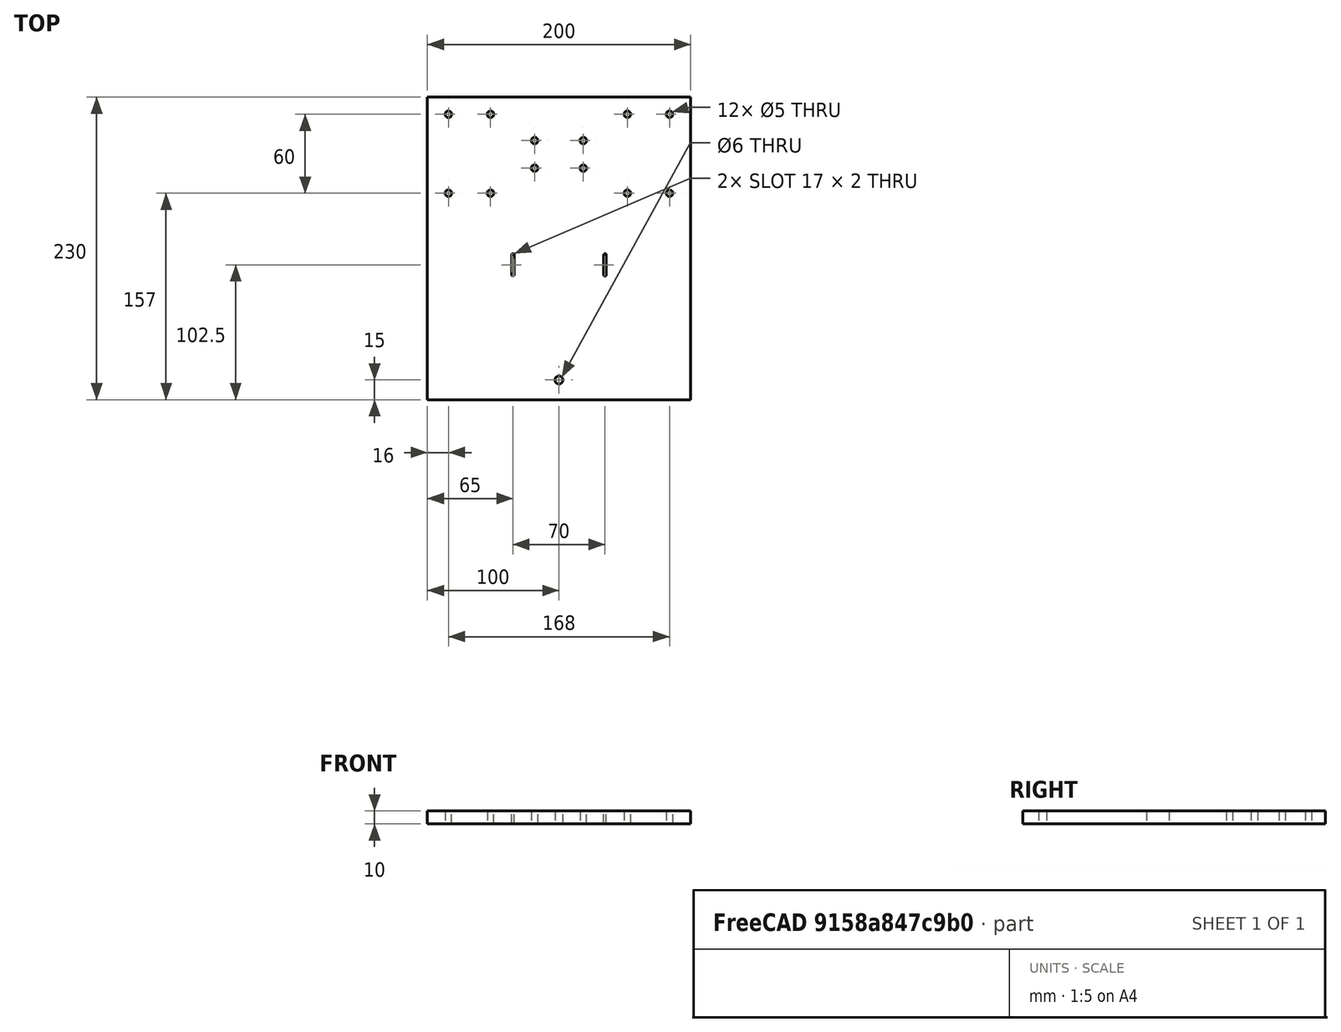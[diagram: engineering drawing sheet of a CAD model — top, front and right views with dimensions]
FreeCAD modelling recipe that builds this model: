
FCSTD DOCUMENT  (FreeCAD 0.15R4664 (Git))
Label: platez_base
License: CC-BY 3.0
LicenseURL: http://creativecommons.org/licenses/by/3.0/
objects: Drawing::FeatureView×38, Sketcher::SketchObject×1, PartDesign::Pad×1, Drawing::FeatureViewPart×1, Drawing::FeaturePage×1
note: 3 computed .brp shape members not serialized (recipe doc carries the construction recipe); baked Part::Feature solids carry a one-line shape summary decoded from their .brp

FEATURE [Sketcher::SketchObject] Sketch
  sketch-geometry (25):
    g0: LineSegment StartX=-100 StartY=230 StartZ=0 EndX=100 EndY=230 EndZ=0
    g1: LineSegment StartX=100 StartY=230 StartZ=0 EndX=100 EndY=0 EndZ=0
    g2: LineSegment StartX=100 StartY=0 StartZ=0 EndX=-100 EndY=0 EndZ=0
    g3: LineSegment StartX=-100 StartY=0 StartZ=0 EndX=-100 EndY=230 EndZ=0
    g4: Circle CenterX=0 CenterY=15 CenterZ=0 NormalX=0 NormalY=0 NormalZ=1 Radius=3
    g5: ArcOfCircle CenterX=35 CenterY=110 CenterZ=0 NormalX=0 NormalY=0 NormalZ=1 Radius=1 StartAngle=4.4411e-08 EndAngle=3.14159
    g6: LineSegment StartX=36 StartY=110 StartZ=0 EndX=36 EndY=95 EndZ=0
    g7: LineSegment StartX=34 StartY=110 StartZ=0 EndX=34 EndY=95 EndZ=0
    g8: ArcOfCircle CenterX=35 CenterY=95 CenterZ=0 NormalX=0 NormalY=0 NormalZ=1 Radius=1 StartAngle=3.14159 EndAngle=6.28319
    g9: ArcOfCircle CenterX=-35 CenterY=110 CenterZ=0 NormalX=0 NormalY=0 NormalZ=1 Radius=1 StartAngle=6.28319 EndAngle=9.42478
    g10: LineSegment StartX=-34 StartY=110 StartZ=0 EndX=-34 EndY=95 EndZ=0
    g11: LineSegment StartX=-36 StartY=110 StartZ=0 EndX=-36 EndY=95 EndZ=0
    g12: ArcOfCircle CenterX=-35 CenterY=95 CenterZ=0 NormalX=0 NormalY=0 NormalZ=1 Radius=1 StartAngle=3.14159 EndAngle=6.28319
    g13: Circle CenterX=84 CenterY=217 CenterZ=0 NormalX=0 NormalY=0 NormalZ=1 Radius=2.5
    g14: Circle CenterX=84 CenterY=157 CenterZ=0 NormalX=0 NormalY=0 NormalZ=1 Radius=2.5
    g15: Circle CenterX=52 CenterY=157 CenterZ=0 NormalX=0 NormalY=0 NormalZ=1 Radius=2.5
    g16: Circle CenterX=52 CenterY=217 CenterZ=0 NormalX=0 NormalY=0 NormalZ=1 Radius=2.5
    g17: Circle CenterX=-84 CenterY=217 CenterZ=0 NormalX=0 NormalY=0 NormalZ=1 Radius=2.5
    g18: Circle CenterX=-52 CenterY=217 CenterZ=0 NormalX=0 NormalY=0 NormalZ=1 Radius=2.5
    g19: Circle CenterX=-84 CenterY=157 CenterZ=0 NormalX=0 NormalY=0 NormalZ=1 Radius=2.5
    g20: Circle CenterX=-52 CenterY=157 CenterZ=0 NormalX=0 NormalY=0 NormalZ=1 Radius=2.5
    g21: Circle CenterX=-18.5 CenterY=197 CenterZ=0 NormalX=0 NormalY=0 NormalZ=1 Radius=2.5
    g22: Circle CenterX=18.5 CenterY=197 CenterZ=0 NormalX=0 NormalY=0 NormalZ=1 Radius=2.5
    g23: Circle CenterX=-18.5 CenterY=176 CenterZ=0 NormalX=0 NormalY=0 NormalZ=1 Radius=2.5
    g24: Circle CenterX=18.5 CenterY=176 CenterZ=0 NormalX=0 NormalY=0 NormalZ=1 Radius=2.5
  constraints (78):
    c: Coincident(g0,g1)
    c: Coincident(g1,g2)
    c: Coincident(g2,g3)
    c: Coincident(g3,g0)
    c: Horizontal(g0)
    c: Horizontal(g2)
    c: Vertical(g1)
    c: Vertical(g3)
    c: PointOnObject(g1,g-1)
    c: Distance(g2,g1) = 200
    c: Distance(g-1,g2) = 100
    c: Distance(g0,g1) = 230
    c: Radius(g4) = 3
    c: PointOnObject(g4,g-2)
    c: Distance(g-1,g4) = 15
    c: Radius(g5) = 1
    c: Coincident(g6,g5)
    c: Vertical(g6)
    c: Tangent(g6,g5)
    c: Coincident(g7,g5)
    c: Vertical(g7)
    c: Tangent(g7,g5)
    c: Coincident(g8,g7)
    c: Coincident(g8,g6)
    c: Radius(g8) = 1
    c: Distance(g7) = 15
    c: Distance(g7,g6) = 2
    c: Distance(g6,g1) = 64
    c: Distance(g6,g2) = 95
    c: Coincident(g10,g9)
    c: Vertical(g10)
    c: Tangent(g10,g9)
    c: Radius(g9) = 1
    c: Coincident(g11,g9)
    c: Vertical(g11)
    c: Tangent(g11,g9)
    c: Coincident(g12,g11)
    c: Coincident(g12,g10)
    c: Radius(g12) = 1
    c: Distance(g11,g10) = 2
    c: Distance(g10,g2) = 95
    c: Distance(g11,g3) = 64
    c: Radius(g13) = 2.5
    c: Distance(g13,g1) = 16
    c: Distance(g13,g0) = 13
    c: Radius(g14) = 2.5
    c: DistanceY(g13,g14) = -60
    c: Distance(g14,g1) = 16
    c: Radius(g15) = 2.5
    c: DistanceX(g15,g14) = 32
    c: Radius(g16) = 2.5
    c: DistanceX(g16,g13) = 32
    c: Distance(g16,g0) = 13
    c: DistanceY(g16,g15) = -60
    c: Radius(g17) = 2.5
    c: Distance(g17,g0) = 13
    c: Distance(g17,g3) = 16
    c: Radius(g18) = 2.5
    c: Distance(g18,g0) = 13
    c: DistanceY(g17,g19) = -60
    c: Distance(g19,g3) = 16
    c: DistanceY(g18,g20) = -60
    c: DistanceX(g19,g20) = 32
    c: DistanceX(g17,g18) = 32
    c: Radius(g19) = 2.5
    c: Radius(g20) = 2.5
    c: Radius(g21) = 2.5
    c: Radius(g22) = 2.5
    c: Radius(g23) = 2.5
    c: Radius(g24) = 2.5
    c: Distance(g21,g23) = 21
    c: Distance(g22,g24) = 21
    c: Distance(g21,g0) = 33
    c: Distance(g22,g0) = 33
    c: Distance(g21,g3) = 81.5
    c: Distance(g23,g3) = 81.5
    c: Distance(g22,g1) = 81.5
    c: Distance(g24,g1) = 81.5
FEATURE [PartDesign::Pad] Pad
  Length = 10
  Length2 = 1
  Sketch = -> Sketch
  Type = 0
FEATURE [Drawing::FeatureViewPart] View
  Direction = (0,0,1)
  HiddenWidth = 0.15
  LineWidth = 0.35
  Rotation = 0
  Scale = 0.5
  ShowHiddenLines = false
  ShowSmoothLines = false
  Source = -> Pad
  Tolerance = 0.05
  ViewResult = <g id="View"\n   transform="rotate(0,150,140) translate(150,140) scale(0.5,0.5)"\n  >\n<g   stroke="rgb(0, 0, 0)"\n   stroke-width="0.7"\n   stroke-linecap="butt"\n   stroke-linejoin="miter"\n   fill="none"\n   transform="scale(1,-1)"\n  >\n<path id= "1" d=" M -100 230 L 100 230 " />\n<path id= "2" d=" M 100 230 L 100 0 " />\n<path id= "3" d=" M 100 0 L -100 0 " />\n<path id= "4" d=" M -100 0 L -100 230 " />\n<path d="M36 110 A1 1 0 1 1 34 110" /><path id= "6" d=" M 34 110 L 34 95 " />\n<path d="M34 95 A1 1 0 1 1 36 95" /><path id= "8" d=" M 36 110 L 36 95 " />\n<path d="M-34 110 A1 1 0 1 1 -36 110" /><path id= "10" d=" M -36 110 L -36 95 " />\n<path d="M-36 95 A1 1 0 0 1 -34 95" /><path id= "12" d=" M -34 110 L -34 95 " />\n<circle cx ="0" cy ="15" r ="3" /><circle cx ="-52" cy ="157" r ="2.5" /><circle cx ="-84" cy ="157" r ="2.5" /><circle cx ="-52" cy ="217" r ="2.5" /><circle cx ="-84" cy ="217" r ="2.5" /><circle cx ="52" cy ="217" r ="2.5" /><circle cx ="52" cy ="157" r ="2.5" /><circle cx ="84" cy ="157" r ="2.5" /><circle cx ="84" cy ="217" r ="2.5" /><circle cx ="18.5" cy ="176" r ="2.5" /><circle cx ="-18.5" cy ="176" r ="2.5" /><circle cx ="18.5" cy ="197" r ="2.5" /><circle cx ="-18.5" cy ="197" r ="2.5" /></g>\n</g>
  Visible = true
  X = 150
  Y = 140
FEATURE [Drawing::FeatureView] centerLines001
  Rotation = 0
  ViewResult = <g  transform="scale(0.500000,0.500000)" stroke="rgb(0,0,255)"  stroke-width="0.600000" >\n<path d="M 213.500000,63.000000 L 217.500000,63.000000 M 221.500000,63.000000 L 233.500000,63.000000 M 237.500000,63.000000 L 241.500000,63.000000 M 245.500000,63.000000 L 257.500000,63.000000 M 261.500000,63.000000 L 265.500000,63.000000 M 269.500000,63.000000 L 281.500000,63.000000 M 285.500000,63.000000 L 289.500000,63.000000 M 293.500000,63.000000 L 305.500000,63.000000 M 309.500000,63.000000 L 313.500000,63.000000 M 317.500000,63.000000 L 329.500000,63.000000 M 333.500000,63.000000 L 337.500000,63.000000 M 341.500000,63.000000 L 353.500000,63.000000 M 357.500000,63.000000 L 361.500000,63.000000 M 365.500000,63.000000 L 377.500000,63.000000 M 381.500000,63.000000 L 385.500000,63.000000 M 389.500000,63.000000 L 391.658226,63.000000 "/>\n<path d="M 213.500000,63.000000 L 209.500000,63.000000 "/>\n</g> 
  Visible = true
  X = 0
  Y = 0
FEATURE [Drawing::FeatureView] centerLines002
  Rotation = 0
  ViewResult = <g  transform="scale(0.500000,0.500000)" stroke="rgb(0,0,255)"  stroke-width="0.600000" >\n<path d="M 213.500000,123.000000 L 217.500000,123.000000 M 221.500000,123.000000 L 233.500000,123.000000 M 237.500000,123.000000 L 241.500000,123.000000 M 245.500000,123.000000 L 257.500000,123.000000 M 261.500000,123.000000 L 265.500000,123.000000 M 269.500000,123.000000 L 281.500000,123.000000 M 285.500000,123.000000 L 289.500000,123.000000 M 293.500000,123.000000 L 305.500000,123.000000 M 309.500000,123.000000 L 313.500000,123.000000 M 317.500000,123.000000 L 329.500000,123.000000 M 333.500000,123.000000 L 337.500000,123.000000 M 341.500000,123.000000 L 353.500000,123.000000 M 357.500000,123.000000 L 361.500000,123.000000 M 365.500000,123.000000 L 377.500000,123.000000 M 381.500000,123.000000 L 385.500000,123.000000 M 389.500000,123.000000 L 391.945998,123.000000 "/>\n<path d="M 213.500000,123.000000 L 209.500000,123.000000 "/>\n</g> 
  Visible = true
  X = 0
  Y = 0
FEATURE [Drawing::FeatureView] centerLines003
  Rotation = 0
  ViewResult = <g  transform="scale(0.500000,0.500000)" stroke="rgb(0,0,255)"  stroke-width="0.600000" >\n<path d="M 278.750000,83.000000 L 282.750000,83.000000 M 286.750000,83.000000 L 298.750000,83.000000 M 302.750000,83.000000 L 306.750000,83.000000 M 310.750000,83.000000 L 322.750000,83.000000 "/>\n<path d="M 278.750000,83.000000 L 274.750000,83.000000 "/>\n</g> 
  Visible = true
  X = 0
  Y = 0
FEATURE [Drawing::FeatureView] centerLines004
  Rotation = 0
  ViewResult = <g  transform="scale(0.500000,0.500000)" stroke="rgb(0,0,255)"  stroke-width="0.600000" >\n<path d="M 278.750000,104.500000 L 282.750000,104.500000 M 286.750000,104.500000 L 298.750000,104.500000 M 302.750000,104.500000 L 306.750000,104.500000 M 310.750000,104.500000 L 322.750000,104.500000 "/>\n<path d="M 278.750000,104.500000 L 274.750000,104.500000 "/>\n</g> 
  Visible = true
  X = 0
  Y = 0
FEATURE [Drawing::FeatureView] centerLines005
  Rotation = 0
  ViewResult = <g  transform="scale(0.500000,0.500000)" stroke="rgb(0,0,255)"  stroke-width="0.600000" >\n<path d="M 216.000000,60.500000 L 216.000000,64.500000 M 216.000000,68.500000 L 216.000000,80.500000 M 216.000000,84.500000 L 216.000000,88.500000 M 216.000000,92.500000 L 216.000000,104.500000 M 216.000000,108.500000 L 216.000000,112.500000 M 216.000000,116.500000 L 216.000000,128.500000 "/>\n<path d="M 216.000000,60.500000 L 216.000000,56.500000 "/>\n</g> 
  Visible = true
  X = 0
  Y = 0
FEATURE [Drawing::FeatureView] centerLines006
  Rotation = 0
  ViewResult = <g  transform="scale(0.500000,0.500000)" stroke="rgb(0,0,255)"  stroke-width="0.600000" >\n<path d="M 384.000000,60.500000 L 384.000000,64.500000 M 384.000000,68.500000 L 384.000000,80.500000 M 384.000000,84.500000 L 384.000000,88.500000 M 384.000000,92.500000 L 384.000000,104.500000 M 384.000000,108.500000 L 384.000000,112.500000 M 384.000000,116.500000 L 384.000000,128.500000 "/>\n<path d="M 384.000000,60.500000 L 384.000000,56.500000 "/>\n</g> 
  Visible = true
  X = 0
  Y = 0
FEATURE [Drawing::FeatureView] centerLines007
  Rotation = 0
  ViewResult = <g  transform="scale(0.500000,0.500000)" stroke="rgb(0,0,255)"  stroke-width="0.600000" >\n<path d="M 281.250000,80.500000 L 281.250000,84.500000 M 281.250000,88.500000 L 281.250000,100.500000 M 281.250000,104.500000 L 281.250000,108.500000 "/>\n<path d="M 281.250000,80.500000 L 281.250000,76.500000 "/>\n</g> 
  Visible = true
  X = 0
  Y = 0
FEATURE [Drawing::FeatureView] centerLines008
  Rotation = 0
  ViewResult = <g  transform="scale(0.500000,0.500000)" stroke="rgb(0,0,255)"  stroke-width="0.600000" >\n<path d="M 318.750000,80.500000 L 318.750000,84.500000 M 318.750000,88.500000 L 318.750000,100.500000 M 318.750000,104.500000 L 318.750000,108.500000 "/>\n<path d="M 318.750000,80.500000 L 318.750000,76.500000 "/>\n</g> 
  Visible = true
  X = 0
  Y = 0
FEATURE [Drawing::FeatureView] centerLines009
  Rotation = 0
  ViewResult = <g  transform="scale(0.500000,0.500000)" stroke="rgb(0,0,255)"  stroke-width="0.600000" >\n<path d="M 264.000000,177.500000 L 268.000000,177.500000 M 272.000000,177.500000 L 284.000000,177.500000 M 288.000000,177.500000 L 292.000000,177.500000 M 296.000000,177.500000 L 308.000000,177.500000 M 312.000000,177.500000 L 316.000000,177.500000 M 320.000000,177.500000 L 332.000000,177.500000 M 336.000000,177.500000 L 340.000000,177.500000 "/>\n<path d="M 264.000000,177.500000 L 260.000000,177.500000 "/>\n</g> 
  Visible = true
  X = 0
  Y = 0
FEATURE [Drawing::FeatureView] dim001
  Rotation = 0
  ViewResult = <g   >\n<line x1="132.000000" y1="94.500000" x2="132.000000" y2="100.348281" style="stroke:rgb(0,0,255);stroke-width:0.30" />\n<line x1="133.000000" y1="94.500000" x2="133.000000" y2="100.348281" style="stroke:rgb(0,0,255);stroke-width:0.30" />\n<line x1="132.000000" y1="99.348281" x2="133.000000" y2="99.348281" style="stroke:rgb(0,0,255);stroke-width:0.30" />\n<polygon points="132.000000,99.348281 129.000000,98.348281 128.000000,99.348281 129.000000,100.348281" style="fill:rgb(0,0,255);stroke:rgb(0,0,255);stroke-width:0" /><polygon points="133.000000,99.348281 136.000000,100.348281 137.000000,99.348281 136.000000,98.348281" style="fill:rgb(0,0,255);stroke:rgb(0,0,255);stroke-width:0" />\n<text x="129.221177" y="104.897191" font-family="Verdana" font-size="3.6" fill="rgb(255,0,0)" text-anchor="inherit"  >2mm</text>\n</g> 
  Visible = true
  X = 0
  Y = 0
FEATURE [Drawing::FeatureView] dim002
  Rotation = 0
  ViewResult = <g   >\n<line x1="167.000000" y1="94.500000" x2="167.000000" y2="100.120244" style="stroke:rgb(0,0,255);stroke-width:0.30" />\n<line x1="168.000000" y1="94.500000" x2="168.000000" y2="100.120244" style="stroke:rgb(0,0,255);stroke-width:0.30" />\n<line x1="167.000000" y1="99.120244" x2="168.000000" y2="99.120244" style="stroke:rgb(0,0,255);stroke-width:0.30" />\n<polygon points="167.000000,99.120244 164.000000,98.120244 163.000000,99.120244 164.000000,100.120244" style="fill:rgb(0,0,255);stroke:rgb(0,0,255);stroke-width:0" /><polygon points="168.000000,99.120244 171.000000,100.120244 172.000000,99.120244 171.000000,98.120244" style="fill:rgb(0,0,255);stroke:rgb(0,0,255);stroke-width:0" />\n<text x="164.642982" y="104.669153" font-family="Verdana" font-size="3.6" fill="rgb(255,0,0)" text-anchor="inherit"  >2mm</text>\n</g> 
  Visible = true
  X = 0
  Y = 0
FEATURE [Drawing::FeatureView] centerLines010
  Rotation = 0
  ViewResult = <g  transform="scale(0.500000,0.500000)" stroke="rgb(0,0,255)"  stroke-width="0.600000" >\n<path d="M 300.000000,265.000000 L 300.000000,269.000000 "/>\n<path d="M 300.000000,265.000000 L 304.000000,265.000000 "/>\n<path d="M 300.000000,265.000000 L 300.000000,261.000000 "/>\n<path d="M 300.000000,265.000000 L 296.000000,265.000000 "/>\n</g> 
  Visible = true
  X = 0
  Y = 0
FEATURE [Drawing::FeatureView] dim003
  Rotation = 0
  ViewResult = <g   >\n<line x1="197.829113" y1="31.500000" x2="207.218755" y2="31.500000" style="stroke:rgb(0,0,255);stroke-width:0.30" />\n<line x1="197.972999" y1="61.500000" x2="207.218755" y2="61.500000" style="stroke:rgb(0,0,255);stroke-width:0.30" />\n<line x1="206.218755" y1="31.500000" x2="206.218755" y2="61.500000" style="stroke:rgb(0,0,255);stroke-width:0.30" />\n<polygon points="206.218755,31.500000 205.218755,34.500000 206.218755,35.500000 207.218755,34.500000" style="fill:rgb(0,0,255);stroke:rgb(0,0,255);stroke-width:0" /><polygon points="206.218755,61.500000 207.218755,58.500000 206.218755,57.500000 205.218755,58.500000" style="fill:rgb(0,0,255);stroke:rgb(0,0,255);stroke-width:0" />\n<text x="210.925447" y="55.385717" font-family="Verdana" font-size="3.6" fill="rgb(255,0,0)" text-anchor="inherit" transform="rotate(-90.000000 210.925447,55.385717)" >60mm</text>\n</g> 
  Visible = true
  X = 0
  Y = 0
FEATURE [Drawing::FeatureView] dim004
  Rotation = 0
  ViewResult = <g   >\n<line x1="124.000000" y1="28.250000" x2="124.000000" y2="19.705793" style="stroke:rgb(0,0,255);stroke-width:0.30" />\n<line x1="108.000000" y1="26.250000" x2="108.000000" y2="19.705793" style="stroke:rgb(0,0,255);stroke-width:0.30" />\n<line x1="124.000000" y1="20.705793" x2="108.000000" y2="20.705793" style="stroke:rgb(0,0,255);stroke-width:0.30" />\n<polygon points="124.000000,20.705793 121.000000,19.705793 120.000000,20.705793 121.000000,21.705793" style="fill:rgb(0,0,255);stroke:rgb(0,0,255);stroke-width:0" /><polygon points="108.000000,20.705793 111.000000,21.705793 112.000000,20.705793 111.000000,19.705793" style="fill:rgb(0,0,255);stroke:rgb(0,0,255);stroke-width:0" />\n<text x="111.885906" y="18.440455" font-family="Verdana" font-size="3.6" fill="rgb(255,0,0)" text-anchor="inherit"  >32mm</text>\n</g> 
  Visible = true
  X = 0
  Y = 0
FEATURE [Drawing::FeatureView] centerLines011
  Rotation = 0
  ViewResult = <g  transform="scale(0.500000,0.500000)" stroke="rgb(0,0,255)"  stroke-width="0.600000" >\n<path d="M 248.000000,60.500000 L 248.000000,64.500000 M 248.000000,68.500000 L 248.000000,80.500000 M 248.000000,84.500000 L 248.000000,88.500000 M 248.000000,92.500000 L 248.000000,104.500000 M 248.000000,108.500000 L 248.000000,112.500000 M 248.000000,116.500000 L 248.000000,128.500000 "/>\n<path d="M 248.000000,60.500000 L 248.000000,58.705568 "/>\n</g> 
  Visible = true
  X = 0
  Y = 0
FEATURE [Drawing::FeatureView] centerLines012
  Rotation = 0
  ViewResult = <g  transform="scale(0.500000,0.500000)" stroke="rgb(0,0,255)"  stroke-width="0.600000" >\n<path d="M 352.000000,60.500000 L 352.000000,64.500000 M 352.000000,68.500000 L 352.000000,80.500000 M 352.000000,84.500000 L 352.000000,88.500000 M 352.000000,92.500000 L 352.000000,104.500000 M 352.000000,108.500000 L 352.000000,112.500000 M 352.000000,116.500000 L 352.000000,128.500000 "/>\n<path d="M 352.000000,60.500000 L 352.000000,56.500000 "/>\n</g> 
  Visible = true
  X = 0
  Y = 0
FEATURE [Drawing::FeatureView] dim005
  Rotation = 0
  ViewResult = <g   >\n<line x1="176.000000" y1="26.250000" x2="176.000000" y2="20.007385" style="stroke:rgb(0,0,255);stroke-width:0.30" />\n<line x1="192.000000" y1="26.250000" x2="192.000000" y2="20.007385" style="stroke:rgb(0,0,255);stroke-width:0.30" />\n<line x1="176.000000" y1="21.007385" x2="192.000000" y2="21.007385" style="stroke:rgb(0,0,255);stroke-width:0.30" />\n<polygon points="176.000000,21.007385 179.000000,22.007385 180.000000,21.007385 179.000000,20.007385" style="fill:rgb(0,0,255);stroke:rgb(0,0,255);stroke-width:0" /><polygon points="192.000000,21.007385 189.000000,20.007385 188.000000,21.007385 189.000000,22.007385" style="fill:rgb(0,0,255);stroke:rgb(0,0,255);stroke-width:0" />\n<text x="177.824000" y="18.796832" font-family="Verdana" font-size="3.6" fill="rgb(255,0,0)" text-anchor="inherit"  >32mm</text>\n</g> 
  Visible = true
  X = 0
  Y = 0
FEATURE [Drawing::FeatureView] dim007
  Rotation = 0
  ViewResult = <g   >\n<line x1="108.000000" y1="26.250000" x2="108.000000" y2="19.805765" style="stroke:rgb(0,0,255);stroke-width:0.30" />\n<line x1="100.000000" y1="23.000000" x2="100.000000" y2="19.805765" style="stroke:rgb(0,0,255);stroke-width:0.30" />\n<line x1="108.000000" y1="20.805765" x2="100.000000" y2="20.805765" style="stroke:rgb(0,0,255);stroke-width:0.30" />\n<polygon points="108.000000,20.805765 111.000000,21.805765 112.000000,20.805765 111.000000,19.805765" style="fill:rgb(0,0,255);stroke:rgb(0,0,255);stroke-width:0" /><polygon points="100.000000,20.805765 97.000000,19.805765 96.000000,20.805765 97.000000,21.805765" style="fill:rgb(0,0,255);stroke:rgb(0,0,255);stroke-width:0" />\n<text x="97.564510" y="18.796832" font-family="Verdana" font-size="3.6" fill="rgb(255,0,0)" text-anchor="inherit"  >16mm</text>\n</g> 
  Visible = true
  X = 0
  Y = 0
FEATURE [Drawing::FeatureView] dim006
  Rotation = 0
  ViewResult = <g   >\n<line x1="192.000000" y1="26.250000" x2="192.000000" y2="20.025037" style="stroke:rgb(0,0,255);stroke-width:0.30" />\n<line x1="200.000000" y1="23.000000" x2="200.000000" y2="20.025037" style="stroke:rgb(0,0,255);stroke-width:0.30" />\n<line x1="192.000000" y1="21.025037" x2="200.000000" y2="21.025037" style="stroke:rgb(0,0,255);stroke-width:0.30" />\n<polygon points="192.000000,21.025037 189.000000,20.025037 188.000000,21.025037 189.000000,22.025037" style="fill:rgb(0,0,255);stroke:rgb(0,0,255);stroke-width:0" /><polygon points="200.000000,21.025037 203.000000,22.025037 204.000000,21.025037 203.000000,20.025037" style="fill:rgb(0,0,255);stroke:rgb(0,0,255);stroke-width:0" />\n<text x="191.551392" y="19.155139" font-family="Verdana" font-size="3.6" fill="rgb(255,0,0)" text-anchor="inherit"  >16mm</text>\n</g> 
  Visible = true
  X = 0
  Y = 0
FEATURE [Drawing::FeatureView] dim008
  Rotation = 0
  ViewResult = <g   >\n<line x1="163.375000" y1="41.500000" x2="166.828776" y2="41.500000" style="stroke:rgb(0,0,255);stroke-width:0.30" />\n<line x1="163.375000" y1="52.250000" x2="166.828776" y2="52.250000" style="stroke:rgb(0,0,255);stroke-width:0.30" />\n<line x1="165.828776" y1="41.500000" x2="165.828776" y2="52.250000" style="stroke:rgb(0,0,255);stroke-width:0.30" />\n<polygon points="165.828776,41.500000 164.828776,44.500000 165.828776,45.500000 166.828776,44.500000" style="fill:rgb(0,0,255);stroke:rgb(0,0,255);stroke-width:0" /><polygon points="165.828776,52.250000 166.828776,49.250000 165.828776,48.250000 164.828776,49.250000" style="fill:rgb(0,0,255);stroke:rgb(0,0,255);stroke-width:0" />\n<text x="168.474010" y="42.141306" font-family="Verdana" font-size="3.6" fill="rgb(255,0,0)" text-anchor="inherit" transform="rotate(90.000000 168.474010,42.141306)" >21mm</text>\n</g> 
  Visible = true
  X = 0
  Y = 0
FEATURE [Drawing::FeatureView] dim010
  Rotation = 0
  ViewResult = <g   >\n<line x1="124.000000" y1="27.352784" x2="124.000000" y2="20.041257" style="stroke:rgb(0,0,255);stroke-width:0.30" />\n<line x1="176.000000" y1="26.250000" x2="176.000000" y2="20.041257" style="stroke:rgb(0,0,255);stroke-width:0.30" />\n<line x1="124.000000" y1="21.041257" x2="176.000000" y2="21.041257" style="stroke:rgb(0,0,255);stroke-width:0.30" />\n<polygon points="124.000000,21.041257 127.000000,22.041257 128.000000,21.041257 127.000000,20.041257" style="fill:rgb(0,0,255);stroke:rgb(0,0,255);stroke-width:0" /><polygon points="176.000000,21.041257 173.000000,20.041257 172.000000,21.041257 173.000000,22.041257" style="fill:rgb(0,0,255);stroke:rgb(0,0,255);stroke-width:0" />\n<text x="142.965325" y="19.338305" font-family="Verdana" font-size="3.6" fill="rgb(255,0,0)" text-anchor="inherit"  >104mm</text>\n</g> 
  Visible = true
  X = 0
  Y = 0
FEATURE [Drawing::FeatureView] dim011
  Rotation = 0
  ViewResult = <g   >\n<line x1="170.000000" y1="85.000000" x2="173.136543" y2="85.000000" style="stroke:rgb(0,0,255);stroke-width:0.30" />\n<line x1="170.000000" y1="92.500000" x2="173.136543" y2="92.500000" style="stroke:rgb(0,0,255);stroke-width:0.30" />\n<line x1="172.136543" y1="85.000000" x2="172.136543" y2="92.500000" style="stroke:rgb(0,0,255);stroke-width:0.30" />\n<polygon points="172.136543,85.000000 173.136543,82.000000 172.136543,81.000000 171.136543,82.000000" style="fill:rgb(0,0,255);stroke:rgb(0,0,255);stroke-width:0" /><polygon points="172.136543,92.500000 171.136543,95.500000 172.136543,96.500000 173.136543,95.500000" style="fill:rgb(0,0,255);stroke:rgb(0,0,255);stroke-width:0" />\n<text x="176.728962" y="92.112318" font-family="Verdana" font-size="3.6" fill="rgb(255,0,0)" text-anchor="inherit" transform="rotate(-90.000000 176.728962,92.112318)" >15</text>\n</g> 
  Visible = true
  X = 0
  Y = 0
FEATURE [Drawing::FeatureView] centerLines013
  Rotation = 0
  ViewResult = <g  transform="scale(0.500000,0.500000)" stroke="rgb(0,0,255)"  stroke-width="0.600000" >\n<path d="M 264.000000,185.000000 L 268.000000,185.000000 M 272.000000,185.000000 L 284.000000,185.000000 M 288.000000,185.000000 L 292.000000,185.000000 M 296.000000,185.000000 L 308.000000,185.000000 M 312.000000,185.000000 L 316.000000,185.000000 M 320.000000,185.000000 L 332.000000,185.000000 M 336.000000,185.000000 L 338.800893,185.000000 "/>\n<path d="M 264.000000,185.000000 L 261.028889,185.000000 "/>\n</g> 
  Visible = true
  X = 0
  Y = 0
FEATURE [Drawing::FeatureView] centerLines014
  Rotation = 0
  ViewResult = <g  transform="scale(0.500000,0.500000)" stroke="rgb(0,0,255)"  stroke-width="0.600000" >\n<path d="M 264.000000,170.000000 L 268.000000,170.000000 M 272.000000,170.000000 L 284.000000,170.000000 M 288.000000,170.000000 L 292.000000,170.000000 M 296.000000,170.000000 L 308.000000,170.000000 M 312.000000,170.000000 L 316.000000,170.000000 M 320.000000,170.000000 L 332.000000,170.000000 M 336.000000,170.000000 L 338.800893,170.000000 "/>\n<path d="M 264.000000,170.000000 L 260.940911,170.000000 "/>\n</g> 
  Visible = true
  X = 0
  Y = 0
FEATURE [Drawing::FeatureView] dim012
  Rotation = 0
  ViewResult = <g   >\n<line x1="154.000000" y1="132.500000" x2="205.709769" y2="132.500000" style="stroke:rgb(0,0,255);stroke-width:0.30" />\n<line x1="202.000000" y1="140.000000" x2="205.709769" y2="140.000000" style="stroke:rgb(0,0,255);stroke-width:0.30" />\n<line x1="204.709769" y1="132.500000" x2="204.709769" y2="140.000000" style="stroke:rgb(0,0,255);stroke-width:0.30" />\n<polygon points="204.709769,132.500000 205.709769,129.500000 204.709769,128.500000 203.709769,129.500000" style="fill:rgb(0,0,255);stroke:rgb(0,0,255);stroke-width:0" /><polygon points="204.709769,140.000000 203.709769,143.000000 204.709769,144.000000 205.709769,143.000000" style="fill:rgb(0,0,255);stroke:rgb(0,0,255);stroke-width:0" />\n<text x="208.853692" y="139.235794" font-family="Verdana" font-size="3.6" fill="rgb(255,0,0)" text-anchor="inherit" transform="rotate(-90.000000 208.853692,139.235794)" >15mm</text>\n</g> 
  Visible = true
  X = 0
  Y = 0
FEATURE [Drawing::FeatureView] dim013
  Rotation = 0
  ViewResult = <g   >\n<line x1="150.000000" y1="136.500000" x2="150.000000" y2="145.646099" style="stroke:rgb(0,0,255);stroke-width:0.30" />\n<line x1="100.000000" y1="142.000000" x2="100.000000" y2="145.646099" style="stroke:rgb(0,0,255);stroke-width:0.30" />\n<line x1="150.000000" y1="144.646099" x2="100.000000" y2="144.646099" style="stroke:rgb(0,0,255);stroke-width:0.30" />\n<polygon points="150.000000,144.646099 147.000000,143.646099 146.000000,144.646099 147.000000,145.646099" style="fill:rgb(0,0,255);stroke:rgb(0,0,255);stroke-width:0" /><polygon points="100.000000,144.646099 103.000000,145.646099 104.000000,144.646099 103.000000,143.646099" style="fill:rgb(0,0,255);stroke:rgb(0,0,255);stroke-width:0" />\n<text x="115.645273" y="148.942518" font-family="Verdana" font-size="3.6" fill="rgb(255,0,0)" text-anchor="inherit" transform="rotate(0.000000 115.645273,148.942518)" >100</text>\n</g> 
  Visible = true
  X = 0
  Y = 0
FEATURE [Drawing::FeatureView] dim014
  Rotation = 0
  ViewResult = <g   >\n<line x1="98.000000" y1="140.000000" x2="94.895662" y2="140.000000" style="stroke:rgb(0,0,255);stroke-width:0.30" />\n<line x1="128.514444" y1="92.500000" x2="94.895662" y2="92.500000" style="stroke:rgb(0,0,255);stroke-width:0.30" />\n<line x1="95.895662" y1="140.000000" x2="95.895662" y2="92.500000" style="stroke:rgb(0,0,255);stroke-width:0.30" />\n<polygon points="95.895662,140.000000 96.895662,137.000000 95.895662,136.000000 94.895662,137.000000" style="fill:rgb(0,0,255);stroke:rgb(0,0,255);stroke-width:0" /><polygon points="95.895662,92.500000 94.895662,95.500000 95.895662,96.500000 96.895662,95.500000" style="fill:rgb(0,0,255);stroke:rgb(0,0,255);stroke-width:0" />\n<text x="94.193372" y="124.456303" font-family="Verdana" font-size="3.6" fill="rgb(255,0,0)" text-anchor="inherit" transform="rotate(-90.000000 94.193372,124.456303)" >95</text>\n</g> 
  Visible = true
  X = 0
  Y = 0
FEATURE [Drawing::FeatureView] dim015
  Rotation = 0
  ViewResult = <g   >\n<line x1="100.000000" y1="138.000000" x2="100.000000" y2="79.103311" style="stroke:rgb(0,0,255);stroke-width:0.30" />\n<line x1="132.000000" y1="83.000000" x2="132.000000" y2="79.103311" style="stroke:rgb(0,0,255);stroke-width:0.30" />\n<line x1="100.000000" y1="80.103311" x2="132.000000" y2="80.103311" style="stroke:rgb(0,0,255);stroke-width:0.30" />\n<polygon points="100.000000,80.103311 103.000000,81.103311 104.000000,80.103311 103.000000,79.103311" style="fill:rgb(0,0,255);stroke:rgb(0,0,255);stroke-width:0" /><polygon points="132.000000,80.103311 129.000000,79.103311 128.000000,80.103311 129.000000,81.103311" style="fill:rgb(0,0,255);stroke:rgb(0,0,255);stroke-width:0" />\n<text x="108.247717" y="78.521229" font-family="Verdana" font-size="3.6" fill="rgb(255,0,0)" text-anchor="inherit"  >64mm</text>\n</g> 
  Visible = true
  X = 0
  Y = 0
FEATURE [Drawing::FeatureView] dim016
  Rotation = 0
  ViewResult = <g   >\n<line x1="200.000000" y1="138.000000" x2="200.000000" y2="74.949113" style="stroke:rgb(0,0,255);stroke-width:0.30" />\n<line x1="168.000000" y1="83.000000" x2="168.000000" y2="74.949113" style="stroke:rgb(0,0,255);stroke-width:0.30" />\n<line x1="200.000000" y1="75.949113" x2="168.000000" y2="75.949113" style="stroke:rgb(0,0,255);stroke-width:0.30" />\n<polygon points="200.000000,75.949113 197.000000,74.949113 196.000000,75.949113 197.000000,76.949113" style="fill:rgb(0,0,255);stroke:rgb(0,0,255);stroke-width:0" /><polygon points="168.000000,75.949113 171.000000,76.949113 172.000000,75.949113 171.000000,74.949113" style="fill:rgb(0,0,255);stroke:rgb(0,0,255);stroke-width:0" />\n<text x="177.362400" y="74.618895" font-family="Verdana" font-size="3.6" fill="rgb(255,0,0)" text-anchor="inherit"  >64mm</text>\n</g> 
  Visible = true
  X = 0
  Y = 0
FEATURE [Drawing::FeatureView] dim017
  Rotation = 0
  ViewResult = <g   >\n<line x1="133.000000" y1="83.000000" x2="133.000000" y2="76.785699" style="stroke:rgb(0,0,255);stroke-width:0.30" />\n<line x1="167.000000" y1="83.000000" x2="167.000000" y2="76.785699" style="stroke:rgb(0,0,255);stroke-width:0.30" />\n<line x1="133.000000" y1="77.785699" x2="167.000000" y2="77.785699" style="stroke:rgb(0,0,255);stroke-width:0.30" />\n<polygon points="133.000000,77.785699 136.000000,78.785699 137.000000,77.785699 136.000000,76.785699" style="fill:rgb(0,0,255);stroke:rgb(0,0,255);stroke-width:0" /><polygon points="167.000000,77.785699 164.000000,76.785699 163.000000,77.785699 164.000000,78.785699" style="fill:rgb(0,0,255);stroke:rgb(0,0,255);stroke-width:0" />\n<text x="142.040434" y="76.744856" font-family="Verdana" font-size="3.6" fill="rgb(255,0,0)" text-anchor="inherit"  >68mm</text>\n</g> 
  Visible = true
  X = 0
  Y = 0
FEATURE [Drawing::FeatureView] dim018
  Rotation = 0
  ViewResult = <g   >\n<line x1="140.625000" y1="56.250000" x2="140.625000" y2="67.956734" style="stroke:rgb(0,0,255);stroke-width:0.30" />\n<line x1="100.000000" y1="27.000000" x2="100.000000" y2="67.956734" style="stroke:rgb(0,0,255);stroke-width:0.30" />\n<line x1="140.625000" y1="66.956734" x2="100.000000" y2="66.956734" style="stroke:rgb(0,0,255);stroke-width:0.30" />\n<polygon points="140.625000,66.956734 137.625000,65.956734 136.625000,66.956734 137.625000,67.956734" style="fill:rgb(0,0,255);stroke:rgb(0,0,255);stroke-width:0" /><polygon points="100.000000,66.956734 103.000000,67.956734 104.000000,66.956734 103.000000,65.956734" style="fill:rgb(0,0,255);stroke:rgb(0,0,255);stroke-width:0" />\n<text x="112.124158" y="71.269202" font-family="Verdana" font-size="3.6" fill="rgb(255,0,0)" text-anchor="inherit"  >81.5mm</text>\n</g> 
  Visible = true
  X = 0
  Y = 0
FEATURE [Drawing::FeatureView] dim019
  Rotation = 0
  ViewResult = <g   >\n<line x1="159.375000" y1="56.250000" x2="159.375000" y2="67.578448" style="stroke:rgb(0,0,255);stroke-width:0.30" />\n<line x1="200.000000" y1="27.000000" x2="200.000000" y2="67.578448" style="stroke:rgb(0,0,255);stroke-width:0.30" />\n<line x1="159.375000" y1="66.578448" x2="200.000000" y2="66.578448" style="stroke:rgb(0,0,255);stroke-width:0.30" />\n<polygon points="159.375000,66.578448 162.375000,67.578448 163.375000,66.578448 162.375000,65.578448" style="fill:rgb(0,0,255);stroke:rgb(0,0,255);stroke-width:0" /><polygon points="200.000000,66.578448 197.000000,65.578448 196.000000,66.578448 197.000000,67.578448" style="fill:rgb(0,0,255);stroke:rgb(0,0,255);stroke-width:0" />\n<text x="172.687848" y="69.983027" font-family="Verdana" font-size="3.6" fill="rgb(255,0,0)" text-anchor="inherit"  >81.5mm</text>\n</g> 
  Visible = true
  X = 0
  Y = 0
FEATURE [Drawing::FeatureView] dim020
  Rotation = 0
  ViewResult = <g   >\n<line x1="98.000000" y1="25.000000" x2="93.382515" y2="25.000000" style="stroke:rgb(0,0,255);stroke-width:0.30" />\n<line x1="135.375000" y1="41.500000" x2="93.382515" y2="41.500000" style="stroke:rgb(0,0,255);stroke-width:0.30" />\n<line x1="94.382515" y1="25.000000" x2="94.382515" y2="41.500000" style="stroke:rgb(0,0,255);stroke-width:0.30" />\n<polygon points="94.382515,25.000000 93.382515,28.000000 94.382515,29.000000 95.382515,28.000000" style="fill:rgb(0,0,255);stroke:rgb(0,0,255);stroke-width:0" /><polygon points="94.382515,41.500000 95.382515,38.500000 94.382515,37.500000 93.382515,38.500000" style="fill:rgb(0,0,255);stroke:rgb(0,0,255);stroke-width:0" />\n<text x="92.869369" y="37.072090" font-family="Verdana" font-size="3.6" fill="rgb(255,0,0)" text-anchor="inherit" transform="rotate(-90.000000 92.869369,37.072090)" >33mm</text>\n</g> 
  Visible = true
  X = 0
  Y = 0
FEATURE [Drawing::FeatureView] dim021
  Rotation = 0
  ViewResult = <g   >\n<line x1="100.000000" y1="142.000000" x2="100.000000" y2="154.955007" style="stroke:rgb(0,0,255);stroke-width:0.30" />\n<line x1="200.000000" y1="142.000000" x2="200.000000" y2="154.955007" style="stroke:rgb(0,0,255);stroke-width:0.30" />\n<line x1="100.000000" y1="153.955007" x2="200.000000" y2="153.955007" style="stroke:rgb(0,0,255);stroke-width:0.30" />\n<polygon points="100.000000,153.955007 103.000000,154.955007 104.000000,153.955007 103.000000,152.955007" style="fill:rgb(0,0,255);stroke:rgb(0,0,255);stroke-width:0" /><polygon points="200.000000,153.955007 197.000000,152.955007 196.000000,153.955007 197.000000,154.955007" style="fill:rgb(0,0,255);stroke:rgb(0,0,255);stroke-width:0" />\n<text x="138.738524" y="159.027168" font-family="Verdana" font-size="3.6" fill="rgb(255,0,0)" text-anchor="inherit"  >200mm</text>\n</g> 
  Visible = true
  X = 0
  Y = 0
FEATURE [Drawing::FeatureView] dim009
  Rotation = 0
  ViewResult = <g   >\n<line x1="140.625000" y1="36.250000" x2="140.625000" y2="35.088545" style="stroke:rgb(0,0,255);stroke-width:0.30" />\n<line x1="159.375000" y1="36.250000" x2="159.375000" y2="35.088545" style="stroke:rgb(0,0,255);stroke-width:0.30" />\n<line x1="140.625000" y1="36.088545" x2="159.375000" y2="36.088545" style="stroke:rgb(0,0,255);stroke-width:0.30" />\n<polygon points="140.625000,36.088545 143.625000,37.088545 144.625000,36.088545 143.625000,35.088545" style="fill:rgb(0,0,255);stroke:rgb(0,0,255);stroke-width:0" /><polygon points="159.375000,36.088545 156.375000,35.088545 155.375000,36.088545 156.375000,37.088545" style="fill:rgb(0,0,255);stroke:rgb(0,0,255);stroke-width:0" />\n<text x="144.808123" y="35.180657" font-family="Verdana" font-size="3.6" fill="rgb(255,0,0)" text-anchor="inherit"  >37mm</text>\n</g> 
  Visible = true
  X = 0
  Y = 0
FEATURE [Drawing::FeatureView] dim022
  Rotation = 0
  ViewResult = <g   >\n<line x1="202.000000" y1="25.000000" x2="225.666900" y2="25.000000" style="stroke:rgb(0,0,255);stroke-width:0.30" />\n<line x1="202.000000" y1="140.000000" x2="225.666900" y2="140.000000" style="stroke:rgb(0,0,255);stroke-width:0.30" />\n<line x1="224.666900" y1="25.000000" x2="224.666900" y2="140.000000" style="stroke:rgb(0,0,255);stroke-width:0.30" />\n<polygon points="224.666900,25.000000 223.666900,28.000000 224.666900,29.000000 225.666900,28.000000" style="fill:rgb(0,0,255);stroke:rgb(0,0,255);stroke-width:0" /><polygon points="224.666900,140.000000 225.666900,137.000000 224.666900,136.000000 223.666900,137.000000" style="fill:rgb(0,0,255);stroke:rgb(0,0,255);stroke-width:0" />\n<text x="229.739061" y="92.193987" font-family="Verdana" font-size="3.6" fill="rgb(255,0,0)" text-anchor="inherit" transform="rotate(-90.000000 229.739061,92.193987)" >230mm</text>\n</g> 
  Visible = true
  X = 0
  Y = 0
FEATURE [Drawing::FeatureView] dim023
  Rotation = 0
  ViewResult = <g   >\n <circle cx ="150.000000" cy ="132.500000" r="0.500000" stroke="none" fill="rgb(0,0,255)" /> \n<line x1="142.537726" y1="122.356928" x2="150.888905" y2="133.708242" style="stroke:rgb(0,0,255);stroke-width:0.30" />\n<polygon points="149.111095,131.291758 148.138779,128.282672 146.740681,128.069781 146.527790,129.467879" style="fill:rgb(0,0,255);stroke:rgb(0,0,255);stroke-width:0" />\n<polygon points="150.888905,133.708242 151.861221,136.717328 153.259319,136.930219 153.472210,135.532121" style="fill:rgb(0,0,255);stroke:rgb(0,0,255);stroke-width:0" />\n<line x1="142.537726" y1="122.356928" x2="125.768582" y2="122.356928" style="stroke:rgb(0,0,255);stroke-width:0.30" />\n<text x="128.428515" y="121.663032" font-family="Verdana" font-size="3.6" fill="rgb(255,0,0)" text-anchor="inherit"  >6mm</text>\n<!--3.0-->\n<!--Ø%3.3f-->\n</g> 
  Visible = true
  X = 0
  Y = 0
FEATURE [Drawing::FeatureView] dim025
  Rotation = 0
  ViewResult = <g   >\n <circle cx ="108.000000" cy ="61.500000" r="0.500000" stroke="none" fill="rgb(0,0,255)" /> \n<line x1="102.160742" y1="54.728969" x2="108.816348" y2="62.446613" style="stroke:rgb(0,0,255);stroke-width:0.30" />\n<polygon points="107.183652,60.553387 105.981707,57.628438 104.571339,57.524226 104.467127,58.934594" style="fill:rgb(0,0,255);stroke:rgb(0,0,255);stroke-width:0" />\n<polygon points="108.816348,62.446613 110.018293,65.371562 111.428661,65.475774 111.532873,64.065406" style="fill:rgb(0,0,255);stroke:rgb(0,0,255);stroke-width:0" />\n<line x1="102.160742" y1="54.728969" x2="68.772510" y2="54.728969" style="stroke:rgb(0,0,255);stroke-width:0.30" />\n<text x="72.404062" y="52.657499" font-family="Verdana" font-size="3.6" fill="rgb(255,0,0)" text-anchor="inherit"  >12 x 5mm</text>\n<!--2.5-->\n<!--Ø%3.3f-->\n</g> 
  Visible = true
  X = 0
  Y = 0
FEATURE [Drawing::FeaturePage] Page
  EditableTexts = me | myself | my company | type | title | 0001 | 2000-00-00
  Group = -> [View,centerLines001,centerLines002,centerLines003,centerLines004,centerLines005,centerLines006,centerLines007,centerLines008,centerLines009,dim001,dim002,centerLines010,dim003,dim004,centerLines011,centerLines012,dim005,dim007,dim006,dim008,dim010,dim011,centerLines013,centerLines014,dim012,dim013,dim014,dim015,dim016,dim017,dim018,dim019,dim020,dim021,dim009,dim022,dim023,dim025]
  Template = /comum/workspace/FreeCAD/free-cad-code/Build/data/Mod/Drawing/Templates/A4_Landscape_ISO7200.svg
